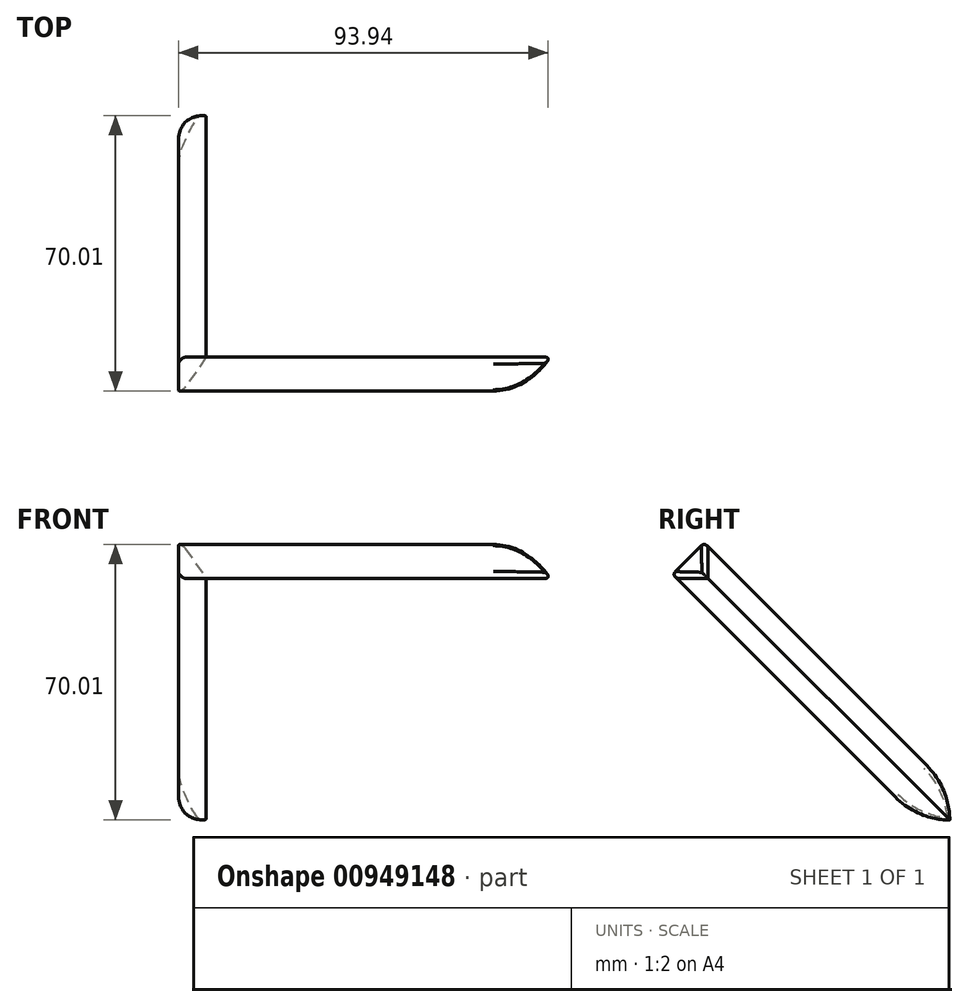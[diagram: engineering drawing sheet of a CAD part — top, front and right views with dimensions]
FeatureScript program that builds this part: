
annotation { "Feature Type Name" : "Feature", "Feature Type Description" : "" }
export const myFeature = defineFeature(function(context is Context, id is Id, definition is map)
    precondition{}
    {
        {
            var Q0;
            Q0=qCreatedBy(makeId("Right.planeOp"),FACE);
            var sketch = newSketch(context, id + "F0", { "sketchPlane" : qUnion([Q0])});
            skLineSegment(sketch, "E0", {"start": v(0, 0) * mm, "end": v(0, 10) * mm});
            skLineSegment(sketch, "E1", {"start": v(0, 10) * mm, "end": v(-10, 0) * mm});
            skLineSegment(sketch, "E2", {"start": v(-10, 0) * mm, "end": v(0, 0) * mm});
            skSolve(sketch);
        }
        {
            var Q0;
            Q0=makeQuery(id+"F0.imprint","IMPRINT",FACE,{"disambiguationData":[TD([[makeQuery(id+"F0.imprint","IMPRINT",EDGE,{"derivedFrom":sQuery(id+"F0.wireOp",EDGE,"E0")}),1.0]])]});
            extrude(context, id + "F1", {"entities" : qUnion([Q0]), "depth" : 100 * mm, "offsetDistance" : 25 * mm});
        }
        {
            var Q0;
            Q0=makeQuery(id+"F1.opExtrude","SWEPT_FACE",FACE,{"disambiguationData":[OSD([sQuery(id+"F0.wireOp",EDGE,"E1")])]});
            var sketch = newSketch(context, id + "F2", { "sketchPlane" : qUnion([Q0])});
            skLineSegment(sketch, "E3", {"start": v(0, 0) * mm, "end": v(100, 0) * mm, "construction": true});
            skLineSegment(sketch, "E4", {"start": v(0, 7.07) * mm, "end": v(7.07, 0) * mm});
            skLineSegment(sketch, "E5", {"start": v(7.07, 0) * mm, "end": v(0, -7.07) * mm});
            skSolve(sketch);
        }
        {
            var Q0;
            Q0 = qSketchRegion(id + "F2", true);
            var Q1;
            Q1=makeQuery(id+"F2.imprint","IMPRINT",FACE,{"disambiguationData":[TD([[makeQuery(id+"F2.imprint","IMPRINT",EDGE,{"derivedFrom":sQuery(id+"F2.wireOp",EDGE,"E4")}),-1.0]])]});
            extrude(context, id + "F3", {"entities" : qUnion([Q0, Q1]), "operationType" : NewBodyOperationType.ADD, "oppositeDirection" : true, "depth" : 100 * mm, "offsetDistance" : 25 * mm});
        }
        {
            var Q0;
            Q0=makeQuery(id+"F1.opExtrude","CAP_EDGE",EDGE,{"disambiguationData":[OSD([sQuery(id+"F0.wireOp",EDGE,"E1")])],"isStart":false});
            var Q1;
            Q1=makeQuery(id+"F3.opExtrude","CAP_EDGE",EDGE,{"disambiguationData":[OSD([sQuery(id+"F0.wireOp",EDGE,"E1")])],"isStart":false});
            fillet(context, id + "F4", {"entities" : qUnion([Q0, Q1]), "radius" : 20 * mm, "tangentPropagation" : true, "allowEdgeOverflow" : false});
        }
        {
            var Q0;
            Q0=makeQuery(id+"F1.opExtrude","SWEPT_EDGE",EDGE,{"disambiguationData":[OSD([sQuery(id+"F0.wireOp",EDGE,"E0"),sQuery(id+"F0.wireOp",EDGE,"E1")])]});
            var Q1;
            Q1=makeQuery(id+"F3.opExtrude","SWEPT_EDGE",EDGE,{"disambiguationData":[OSD([sQuery(id+"F0.wireOp",EDGE,"E0"),sQuery(id+"F0.wireOp",EDGE,"E1"),sQuery(id+"F2.wireOp",EDGE,"E4")])]});
            var Q2;
            Q2=makeQuery(id+"F3.opExtrude","SWEPT_EDGE",EDGE,{"disambiguationData":[OSD([sQuery(id+"F0.wireOp",EDGE,"E1"),sQuery(id+"F0.wireOp",EDGE,"E2"),sQuery(id+"F2.wireOp",EDGE,"E5")])]});
            var Q3;
            Q3=makeQuery(id+"F1.opExtrude","SWEPT_EDGE",EDGE,{"disambiguationData":[OSD([sQuery(id+"F0.wireOp",EDGE,"E1"),sQuery(id+"F0.wireOp",EDGE,"E2")])]});
            fillet(context, id + "F5", {"entities" : qUnion([Q0, Q1, Q2, Q3]), "radius" : 1 * mm, "tangentPropagation" : true, "allowEdgeOverflow" : false});
        }
    });
